# Revit family: Cascade-Systems_Quinta Pro_5-Boilers_Air Dirt Separator_Back-to-Back_v2011
name_source: partatom
category: Mechanical Equipment
revit_build: Autodesk Revit MEP 2012 (Build: 20110309_2315(x64)
units: mm (PartAtom-declared; Revit-internal decimal feet)

## types (5) — shared parameters
Air Supply Pipe Radius = 80.000 mm
Apparent Load = 0 VA
Assembly Code = D3020100
Back Clearance = 1000.000 mm
Between Boilers Clearance = 30.000 mm
Boiler Unit = Metal - Reflective - White
Clearence Box = Glass - Clear - Amber
Combustion Gas Exhaust Pipe Radius = 40.000 mm
Connection Note = If primary connections to low loss header is to the front or rear of the cascade system please view Cascade technical manual for further dimensional clearances.
Controls Voltage = 24 (max 4va)
DN100 Primary 461 - 642kW_Gas Connection_DIN 2633 - 4 hole = DN65
DN100 Primary 461 - 642kW_Primary Flow Connection to Header_PN6 DIN2631-  4 Hole = DN100
DN100 Primary 461 - 642kW_Primary Return Connection to Header_PN6 DIN2631-  4 Hole = DN100
DN100 Primary 461 - 642kW_Secondary Flow Connection to Header_PN6 DIN2631-  4 Hole = DN125
DN100 Primary 461 - 642kW_Secondary Return Connection to Header_PN6 DIN2631-  4 Hole = DN125
DN65 Primary 0 - 460kW_Gas Connection_DIN 2633 - 4 hole = DN50
DN65 Primary 0 - 460kW_Primary Flow Connection to Header_PN6 DIN2631-  4 HolePN6 DIN2631-  4 Hole = DN65
DN65 Primary 0 - 460kW_Primary Return Connection to Header_PN6 DIN2631-  4 HolePN6 DIN2631-  4 Hole = DN65
DN65 Primary 0 - 460kW_Secondary Flow Connection to Header_PN6 DIN2631-  4 Hole = DN100
DN65 Primary 0 - 460kW_Secondary Return Connection to Header_PN6 DIN2631-  4 Hole = DN100
Default Elevation = 0.000 mm
Description = Condensing Boiler
Expansions Vessel Connection = Yes
Filling Valve / Drain Valve = Yes
Flame Protection = Ionisation
Flow Connection Diameter - 35 x 1,5 to Main Pipe = 35.000 mm
Flow Connection Isolating Valve = Yes
Flow Pipe = Paint - Red
Front Clearance = 1000.000 mm
Fuse Rating = 6 A
Gas Connection BSP = 19.050 mm
Gas Connection Isolating Valve = Yes
Gas Connection Pipe Diameter = 19.050 mm
Gas Connection Pipe Radius = 9.525 mm
Gas Pipe = Paint - Yellow
Heating Circuit Flow Diameter = 31.750 mm
Heating Circuit Flow Pipe Radius = 15.875 mm
Heating Circuit Return Pipe Diameter = 31.750 mm
Heating Circuit Return Pipe Radius = 15.875 mm
Host Condition = Wall Hung
Hydraulic-Deaerator_Dirt-Separator = Metal - Brass - Polished
Ignition = Electronic
Installation URL = http://www.remeha.co.uk
Instrument Box Panel = Metal - Polished Silver
Insulation = Insulation - Black
Insulation Class IP = X4D
Insulation Visibility = Yes
Isolating Valve = Yes
Load Classification = Power
Load Sub-Classification Motor = Yes
Low Loss Header Clearance = 650.000 mm
Low Loss Header Clearance DN100 = 650.000 mm
Low Loss Header Clearance DN65 = 650.000 mm
Manufacturer = Remeha Commercial
Manufacturer Fax = 0118 978 6977
Maximum operating pressure  bar = 4 bar
Min / Max gas pressures mbar NG = 17 – 30 mbar
Min Operating Pressure = 0.80 bar
Minimum operating pressure  bar = 0.8 bar
Modulating Input V dc = 0 -10
No Of Boilers = 5
Non Return Valve = Yes
Note = Primary pipework set and low loss header dependant on kW rating of the cascade systerm. Use DN65 on 0 - 460kW systems and Use DN100 on 461 - 642kW
Number of Poles = 1
Optional Fuel = Propane
Power Factor = 1
Power Supply = 230v – 1ph – 50hz
Product Page URL = http://www.remeha.co.uk
Return Connection Diameter - 35 x 1,5 to Main Pipe = 35.000 mm
Return Pipe = Paint - Blue
Safety Valve = Yes
Sales Brochure = http://www.remeha.co.uk
Siphon Bush Pipe Diameter = 19.000 mm
Siphon Bush Pipe Radius = 9.500 mm
Standard Fuel Available = Natural Gas
Standard Operating Temperature = 20 – 90 deg C
Start Current = 2 A
Subcategory = Condensing Boilers
Technical Information URL = http://www.remeha.co.uk
Text Material = Paint - Black
Top Clearance = 400.000 mm
URL = http://www.remeha.co.uk
Voltage = 230 V

## per-type parameters (varying)
- Free-Stand_5-Boiler_Quinta Pro 30: Concentric Connection=80 – 125mm; Efficiency Full load @ 80 / 60 c NCV %=97.50%; Flue Gas temperature deg C=65 deg c; Fuel consumption m3 /hr LPG=1.3 m3/h; Fuel consumption m3/hr Natural Gas=3.3 m3/h; High limit set point  deg C=110 deg c; Low Loss Header_DN 100=No; Low Loss Header_DN 65=Yes; Maximum flue gas flow rate Kg/hr=50 Kg/h; Min / Max gas pressure mbar LPG=37 -  50 mbar; Minimum flow rate m3/hr (water flow)=0.4 m3/hr; Model=Quinta Pro 30; NOx mg/kW dry=37 Mg/kWh; Noise levels dB(A) @1 metre=38dB(A); Nom flow rate @ 20dT l/s=0.35 l/s; Nom flow rate @11dT l/s=0.64 l/s; OV=569.000 mm; Power Consumption Full Load W=39; Power Consumption Part Load W=18; Power Consumption Standby   W=5; Radiated losses @ 30 deg C=0.303; Rated output kW 50 / 30=31.4 kW; Rated output kW 80 / 60=29.3 kW; Resistance @11 deg dT=231 mbar; Resistance at 20 deg dT=70 mbar; Water Content=5.50 L; Weight Kg=53 kgf
- Free-Stand_5-Boiler_Quinta Pro 45: Concentric Connection=80 – 125mm; Efficiency Full load @ 80 / 60 c NCV %=97.20%; Flue Gas temperature deg C=67 deg C; Fuel consumption m3 /hr LPG=1.7 m3/h; Fuel consumption m3/hr Natural Gas=4.4 m3/h; High limit set point  deg C=110 deg C; Low Loss Header_DN 100=No; Low Loss Header_DN 65=Yes; Maximum flue gas flow rate Kg/hr=69 kg/h; Min / Max gas pressure mbar LPG=37 – 50 mbar; Minimum flow rate m3/hr (water flow)=0.4 m3/h; Model=Quinta Pro 45; NOx mg/kW dry=37Mg/kWh; Noise levels dB(A) @1 metre=45 dB(A); Nom flow rate @ 20dT l/s=0.48 l/s; Nom flow rate @11dT l/s=0.87 l/s; OV=569.000 mm; Power Consumption Full Load W=68; Power Consumption Part Load W=18; Power Consumption Standby   W=5; Radiated losses @ 30 deg C=0.245; Rated output kW 50 / 30=43 kW; Rated output kW 80 / 60=40 kW; Resistance @11 deg dT=297 mbar; Resistance at 20 deg dT=90 mbar; Water Content=5.50 L; Weight Kg=53 kgf
- Free-Stand_5-Boiler_Quinta Pro 65: Concentric Connection=100 – 150mm; Efficiency Full load @ 80 / 60 c NCV %=98.30%; Flue Gas temperature deg C=68 deg C; Fuel consumption m3 /hr LPG=2.5 m3/h; Fuel consumption m3/hr Natural Gas=6.6 m3/h; High limit set point  deg C=110 deg C; Low Loss Header_DN 100=No; Low Loss Header_DN 65=Yes; Maximum flue gas flow rate Kg/hr=104 Kg/h; Min / Max gas pressure mbar LPG=37 – 50 mbar; Minimum flow rate m3/hr (water flow)=0.4 m3/h; Model=Quinta Pro 65; NOx mg/kW dry=32 Mg/kWh; Noise levels dB(A) @1 metre=45 dB(A); Nom flow rate @ 20dT l/s=0.77 l/s; Nom flow rate @11dT l/s=1.33 l/s; OV=569.000 mm; Power Consumption Full Load W=88; Power Consumption Part Load W=23; Power Consumption Standby   W=6; Radiated losses @ 30 deg C=0.177; Rated output kW 50 / 30=65 kW; Rated output kW 80 / 60=61 kW; Resistance @11 deg dT=430 mbar; Resistance at 20 deg dT=130 mbar; Water Content=6.50 L; Weight Kg=60 kgf
- Free-Stand_5-Boiler_Quinta Pro 90: Concentric Connection=100 – 150mm; Efficiency Full load @ 80 / 60 c NCV %=97.90%; Flue Gas temperature deg C=68 deg C; Fuel consumption m3 /hr LPG=3.5 m3/h; Fuel consumption m3/hr Natural Gas=9.1 m3/h; High limit set point  deg C=110 deg C; Low Loss Header_DN 100=No; Low Loss Header_DN 65=Yes; Maximum flue gas flow rate Kg/hr=138 Kg/h; Min / Max gas pressure mbar LPG=37 – 50 mbar; Minimum flow rate m3/hr (water flow)=0.4 m3/h; Model=Quinta Pro 90; NOx mg/kW dry=29 Mg/kWh; Noise levels dB(A) @1 metre=52 dB(A); Nom flow rate @ 20dT l/s=1.00 l/s; Nom flow rate @11dT l/s=1.83 l/s; OV=569.000 mm; Power Consumption Full Load W=125; Power Consumption Part Load W=20; Power Consumption Standby   W=4; Radiated losses @ 30 deg C=0.143; Rated output kW 50 / 30=89.5 kW; Rated output kW 80 / 60=84.2 kW; Resistance @11 deg dT=463 mbar; Resistance at 20 deg dT=140 mbar; Water Content=7.50 L; Weight Kg=67 kgf
- Free-Stand_5-Boiler_Quinta Pro 115: Concentric Connection=100 – 150mm; Efficiency Full load @ 80 / 60 c NCV %=96.60%; Flue Gas temperature deg C=72; Fuel consumption m3 /hr LPG=4.7 m3/h; Fuel consumption m3/hr Natural Gas=11.7 m3/h; High limit set point  deg C=110 deg C; Low Loss Header_DN 100=Yes; Low Loss Header_DN 65=No; Maximum flue gas flow rate Kg/hr=178 Kg/h; Min / Max gas pressure mbar LPG=37 – 50 mbar; Minimum flow rate m3/hr (water flow)=0.4 m3/h; Model=Quinta Pro 115; NOx mg/kW dry=35 Mg/kWh; Noise levels dB(A) @1 metre=51 dB(A); Nom flow rate @ 20dT l/s=1.28 l/s; Nom flow rate @11dT l/s=2.22 l/s; OV=875.000 mm; Power Consumption Full Load W=199; Power Consumption Part Load W=45; Power Consumption Standby   W=7; Radiated losses @ 30 deg C=0.112; Rated output kW 50 / 30=114 kW; Rated output kW 80 / 60=107 kW; Resistance @11 deg dT=826 mbar; Resistance at 20 deg dT=250 mbar; Water Content=7.50 L; Weight Kg=68 kgf

## geometry (parser evidence)
native form markers: Blend x18, Sweep x33
no freeform markers — native parametric forms only
